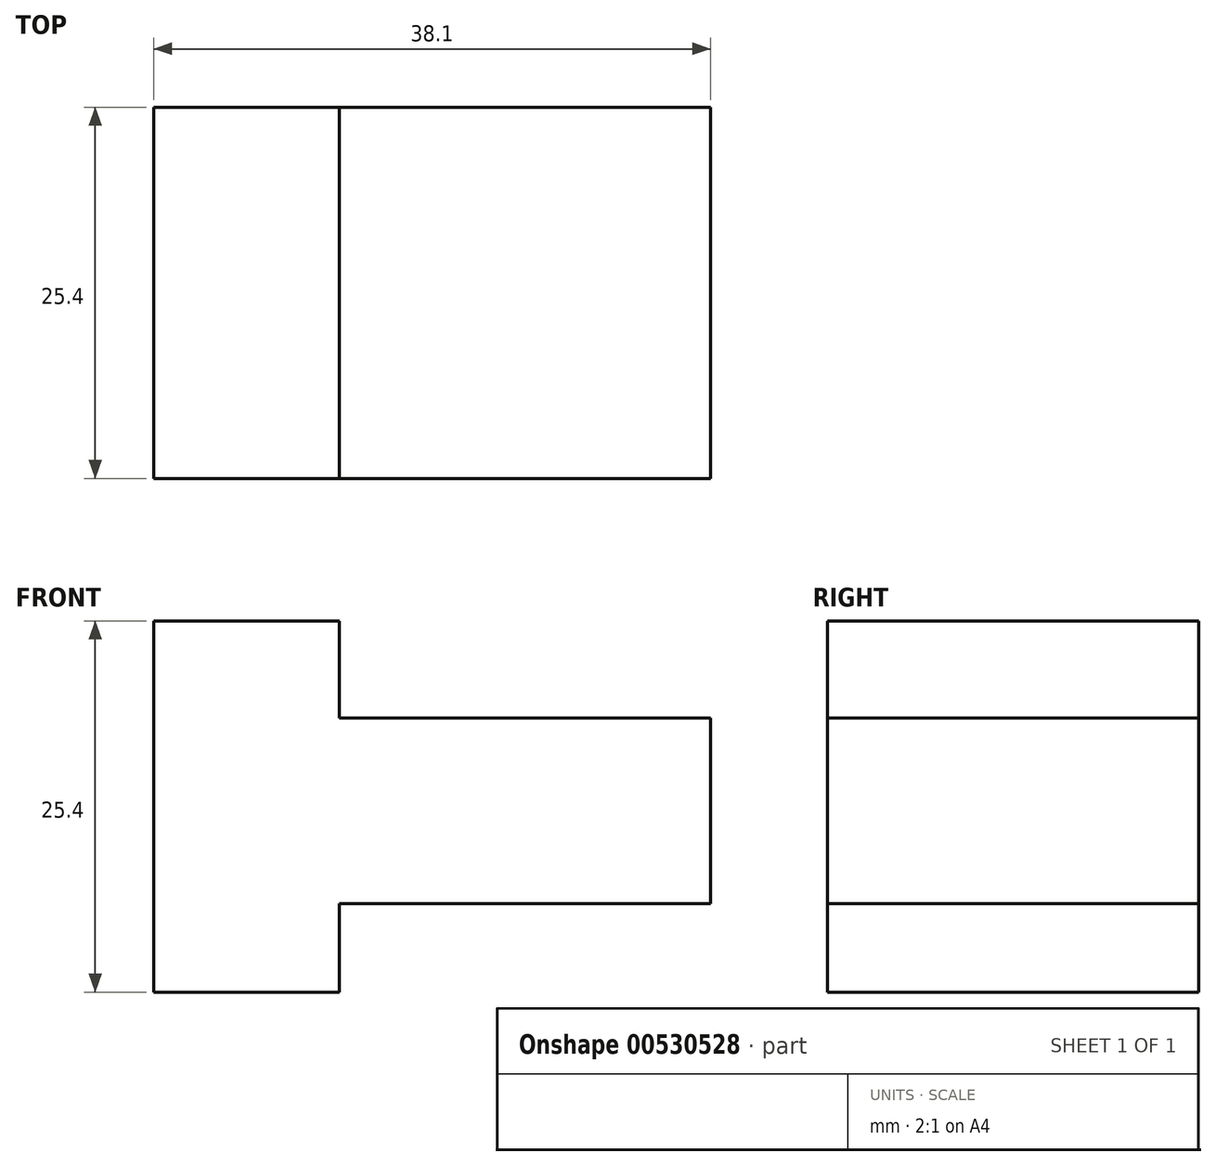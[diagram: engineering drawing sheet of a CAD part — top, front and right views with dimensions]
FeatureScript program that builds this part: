
annotation { "Feature Type Name" : "Feature", "Feature Type Description" : "" }
export const myFeature = defineFeature(function(context is Context, id is Id, definition is map)
    precondition{}
    {
        {
            var Q0;
            Q0=qCreatedBy(makeId("Front.planeOp"),FACE);
            var sketch = newSketch(context, id + "F0", { "sketchPlane" : qUnion([Q0])});
            skLineSegment(sketch, "E0", {"start": v(-91.5, 0) * mm, "end": v(-91.5, 25.4) * mm});
            skLineSegment(sketch, "E1", {"start": v(-91.5, 25.4) * mm, "end": v(-78.8, 25.4) * mm});
            skLineSegment(sketch, "E2", {"start": v(-78.8, 25.4) * mm, "end": v(-78.8, 18.76) * mm});
            skLineSegment(sketch, "E3", {"start": v(-78.8, 18.76) * mm, "end": v(-53.4, 18.76) * mm});
            skLineSegment(sketch, "E4", {"start": v(-53.4, 18.76) * mm, "end": v(-53.4, 6.06) * mm});
            skLineSegment(sketch, "E5", {"start": v(-53.4, 6.06) * mm, "end": v(-78.8, 6.06) * mm});
            skLineSegment(sketch, "E6", {"start": v(-78.8, 6.06) * mm, "end": v(-78.8, 0) * mm});
            skLineSegment(sketch, "E7", {"start": v(-91.5, 0) * mm, "end": v(-78.8, 0) * mm});
            skSolve(sketch);
        }
        {
            var Q0;
            Q0 = qSketchRegion(id + "F0", true);
            extrude(context, id + "F1", {"entities" : qUnion([Q0]), "depth" : 25.4 * mm, "offsetDistance" : 25.4 * mm});
        }
    });
